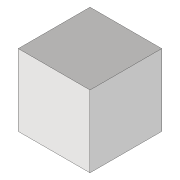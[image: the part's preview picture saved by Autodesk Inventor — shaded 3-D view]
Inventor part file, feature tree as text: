
AUTODESK INVENTOR PART (.ipt)
format: ipt  version: 2020 (Build 240168000, 168)  size: 74,240 bytes
history: native  units: mm
features: extrude x1, sketch x1
ambient origin geometry x8: Origin, YZ Plane, XZ Plane, XY Plane, X Axis, Y Axis, Z Axis, Center Point
bodies: Volumenkörper1 (feature_tree)
feature tree (2):
  extrude  "Extrusion1"  Depth=1.0mm
  sketch  "Skizze1"  dims[d0=1.0mm d1=1.0mm d2=1.0mm d3=0.0mm]
